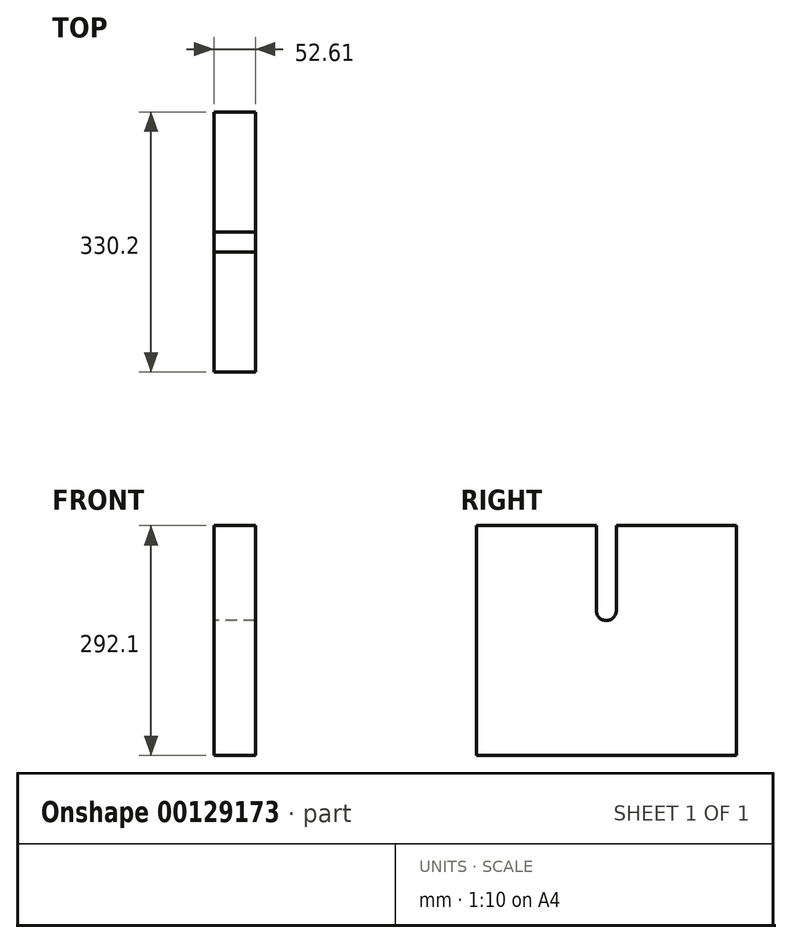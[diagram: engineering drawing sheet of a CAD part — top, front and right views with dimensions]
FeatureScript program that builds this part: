
annotation { "Feature Type Name" : "Feature", "Feature Type Description" : "" }
export const myFeature = defineFeature(function(context is Context, id is Id, definition is map)
    precondition{}
    {
        {
            var Q0;
            Q0=qCreatedBy(makeId("Right.planeOp"),FACE);
            var sketch = newSketch(context, id + "F0", { "sketchPlane" : qUnion([Q0])});
            skLineSegment(sketch, "E0.top", {"start": v(-165.1, -146.05) * mm, "end": v(165.1, -146.05) * mm});
            skLineSegment(sketch, "E0.left", {"start": v(-165.1, 146.05) * mm, "end": v(-165.1, -146.05) * mm});
            skLineSegment(sketch, "E0.right", {"start": v(165.1, 146.05) * mm, "end": v(165.1, -146.05) * mm});
            skPoint(sketch, "E0.middle", {"position": v(0, 0) * mm});
            skLineSegment(sketch, "E1", {"start": v(-165.1, 146.05) * mm, "end": v(-12.7, 146.05) * mm});
            skLineSegment(sketch, "E2.trimOffspring", {"start": v(12.7, 146.05) * mm, "end": v(165.1, 146.05) * mm});
            skLineSegment(sketch, "E3", {"start": v(-12.7, 146.05) * mm, "end": v(-12.7, 38.1) * mm});
            skLineSegment(sketch, "E4", {"start": v(12.7, 146.05) * mm, "end": v(12.7, 38.1) * mm});
            skArc(sketch, "E5", {"start": v(-12.7, 38.1) * mm, "mid": v(0, 25.4) * mm, "end": v(12.7, 38.1) * mm});
            skPoint(sketch, "E6", {"position": v(-127.38, 82.6) * mm});
            skSolve(sketch);
        }
        {
            var Q0;
            Q0=makeQuery(id+"F0.imprint","IMPRINT",FACE,{"disambiguationData":[TD([[makeQuery(id+"F0.imprint","IMPRINT",EDGE,{"derivedFrom":sQuery(id+"F0.wireOp",EDGE,"E0.top")}),1.0]])]});
            extrude(context, id + "F1", {"entities" : qUnion([Q0]), "depth" : 52.6 * mm});
        }
    });
